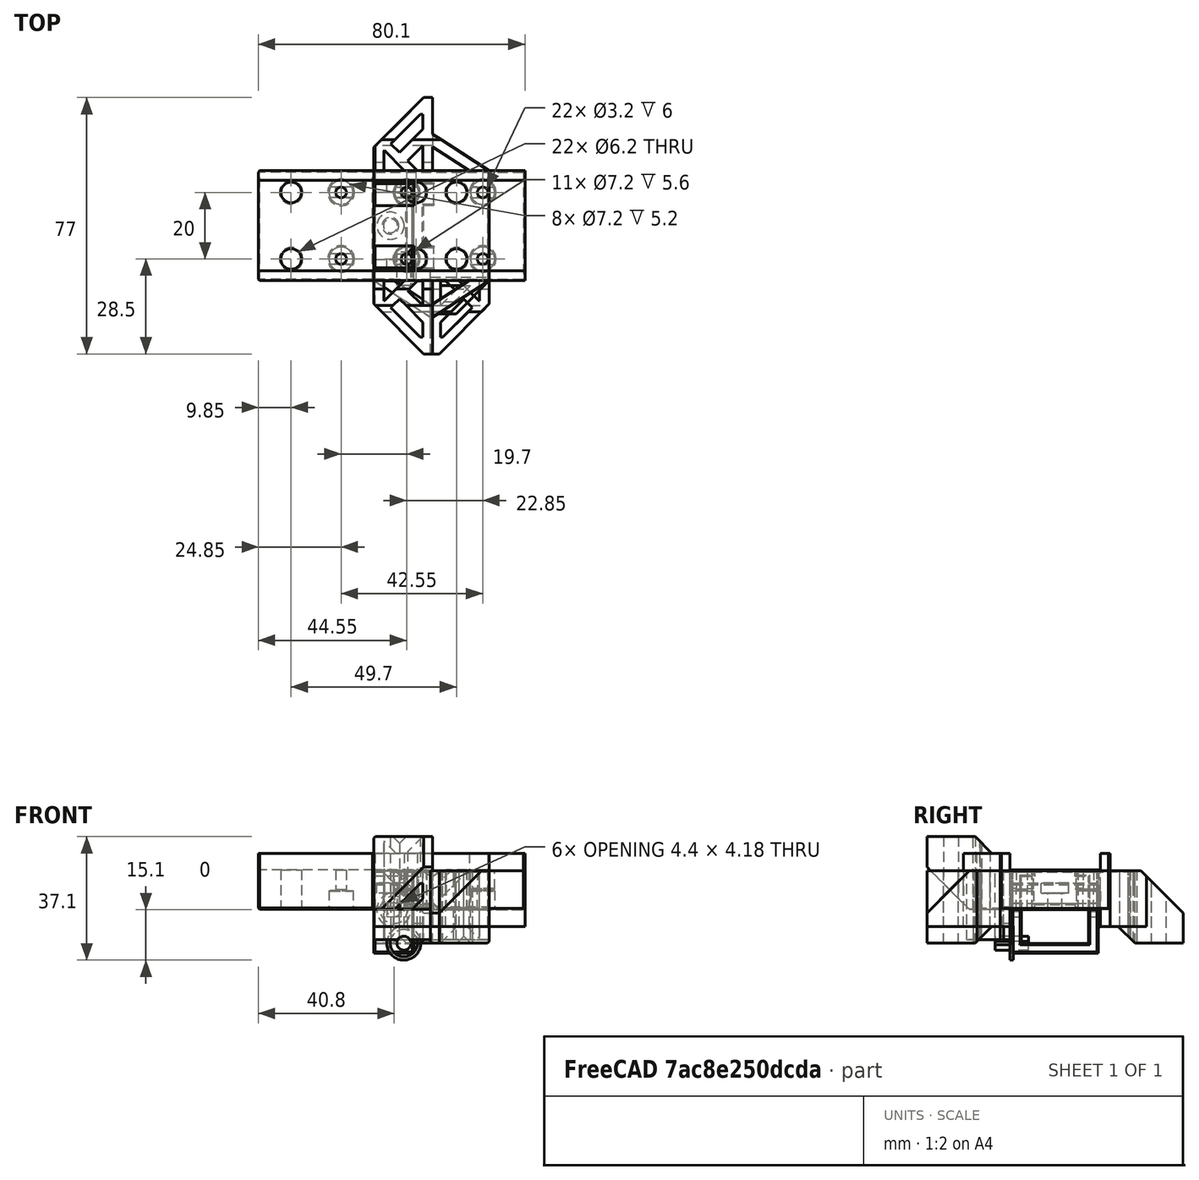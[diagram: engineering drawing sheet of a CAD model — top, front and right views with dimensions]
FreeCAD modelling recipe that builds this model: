
FCSTD DOCUMENT  (FreeCAD 0.18R14555 (Git shallow))
Label: rail-block
License: All rights reserved
LicenseURL: http://en.wikipedia.org/wiki/All_rights_reserved
objects: Part::Box×31, Part::Feature×26, Part::Cut×24, Part::Cylinder×22, Part::MultiFuse×17, Part::Chamfer×15, Part::MultiCommon×1
note: 136 computed .brp shape members not serialized (recipe doc carries the construction recipe); baked Part::Feature solids carry a one-line shape summary decoded from their .brp

FEATURE [Part::Box] Box  label="Cube"
  AttacherType = Attacher::AttachEngine3D
  Height = 2
  Length = 18
  Placement = pos=(0,-13,0) rot=(0,0,1;0rad)
  Width = 26
FEATURE [Part::Box] Box001  label="Cube001"
  AttacherType = Attacher::AttachEngine3D
  Height = 8
  Length = 10
  Placement = pos=(0,-13,0) rot=(0,0,1;0rad)
  Width = 26
FEATURE [Part::Cylinder] Cylinder
  Angle = 360
  AttacherType = Attacher::AttachEngine3D
  Height = 8
  Placement = pos=(5,0,0) rot=(0,0,1;0rad)
  Radius = 2.1
FEATURE [Part::Cylinder] Cylinder001
  Angle = 360
  AttacherType = Attacher::AttachEngine3D
  Height = 3
  Placement = pos=(5,0,5) rot=(0,0,1;0rad)
  Radius = 4.1
FEATURE [Part::Box] Box004  label="Cube004"
  AttacherType = Attacher::AttachEngine3D
  Height = 2
  Length = 3
  Placement = pos=(15,-6.1,0) rot=(0,0,1;0rad)
  Width = 12.2
FEATURE [Part::Box] Box006  label="Cube006"
  AttacherType = Attacher::AttachEngine3D
  Height = 20.2
  Length = 12
  Placement = pos=(0,-10.1,-10.1) rot=(0,0,1;0rad)
  Width = 20.2
FEATURE [Part::Box] Box007  label="Cube007"
  AttacherType = Attacher::AttachEngine3D
  Height = 25
  Length = 12
  Placement = pos=(0,-13,-13) rot=(0,0,1;0rad)
  Width = 26
FEATURE [Part::Cut] Cut002
  Base = -> Box007
  Tool = -> Box006
FEATURE [Part::Box] Box008  label="Cube008"
  AttacherType = Attacher::AttachEngine3D
  Height = 10
  Length = 12
  Placement = pos=(0,-6.05,4) rot=(0,0,1;0rad)
  Width = 12.1
FEATURE [Part::Cut] Cut003
  Base = -> Cut002
  Tool = -> Box008
FEATURE [Part::Cylinder] Cylinder004
  Angle = 360
  AttacherType = Attacher::AttachEngine3D
  Height = 38
  Placement = pos=(6,-18,4e-15) rot=(-1,0,0;1.5708rad)
  Radius = 2.1
FEATURE [Part::Cylinder] Cylinder005
  Angle = 360
  AttacherType = Attacher::AttachEngine3D
  Height = 38
  Placement = pos=(7.8,-18,4e-15) rot=(-1,0,0;1.5708rad)
  Radius = 0.5
FEATURE [Part::MultiFuse] Fusion002
  Shapes = -> [Cylinder004,Cylinder005]
FEATURE [Part::Cut] Cut004  label="node-rev-1-tmp"
  Base = -> Cut003
  Tool = -> Fusion002
FEATURE [Part::Box] Box009  label="Cube009"
  AttacherType = Attacher::AttachEngine3D
  Height = 16.8
  Length = 34.7
  Placement = pos=(0,-16.5,-5) rot=(0,0,1;0rad)
  Width = 33
FEATURE [Part::Box] Box010  label="Cube010"
  AttacherType = Attacher::AttachEngine3D
  Height = 5
  Length = 34.7
  Placement = pos=(0,-13.6,-5) rot=(0,0,1;0rad)
  Width = 27.2
FEATURE [Part::Cylinder] Cylinder006
  Angle = 360
  AttacherType = Attacher::AttachEngine3D
  Height = 12
  Placement = pos=(9.85,10,0) rot=(0,0,1;0rad)
  Radius = 1.6
FEATURE [Part::Cylinder] Cylinder007
  Angle = 360
  AttacherType = Attacher::AttachEngine3D
  Height = 12
  Placement = pos=(9.85,-10,0) rot=(0,0,1;0rad)
  Radius = 1.6
FEATURE [Part::Cylinder] Cylinder008
  Angle = 360
  AttacherType = Attacher::AttachEngine3D
  Height = 12
  Placement = pos=(24.85,10,0) rot=(0,0,1;0rad)
  Radius = 3.1
FEATURE [Part::Cylinder] Cylinder009
  Angle = 360
  AttacherType = Attacher::AttachEngine3D
  Height = 12
  Placement = pos=(24.85,-10,0) rot=(0,0,1;0rad)
  Radius = 3.1
FEATURE [Part::Cylinder] Cylinder010
  Angle = 360
  AttacherType = Attacher::AttachEngine3D
  Height = 6
  Placement = pos=(9.85,-10,6) rot=(0,0,1;0rad)
  Radius = 3.6
FEATURE [Part::Cylinder] Cylinder011
  Angle = 360
  AttacherType = Attacher::AttachEngine3D
  Height = 6
  Placement = pos=(9.85,10,6) rot=(0,0,1;0rad)
  Radius = 3.6
FEATURE [Part::Cylinder] Cylinder012
  Angle = 360
  AttacherType = Attacher::AttachEngine3D
  Height = 10
  Placement = pos=(9,-8,-10) rot=(1,0,0;1.5708rad)
  Radius = 2.1
FEATURE [Part::Cylinder] Cylinder013
  Angle = 360
  AttacherType = Attacher::AttachEngine3D
  Height = 10
  Placement = pos=(10.9,-8,-10) rot=(1,0,0;1.5708rad)
  Radius = 0.5
FEATURE [Part::Cylinder] Cylinder014
  Angle = 360
  AttacherType = Attacher::AttachEngine3D
  Height = 1
  Placement = pos=(9,-12.5,-10) rot=(1,0,0;1.5708rad)
  Radius = 5.1
FEATURE [Part::Cylinder] Cylinder015
  Angle = 360
  AttacherType = Attacher::AttachEngine3D
  Height = 1
  Placement = pos=(9,-12.5,-10) rot=(1,0,0;1.5708rad)
  Radius = 4.1
FEATURE [Part::Cut] Cut
  Base = -> Cylinder014
  Tool = -> Cylinder015
FEATURE [Part::Cylinder] Cylinder016
  Angle = 360
  AttacherType = Attacher::AttachEngine3D
  Height = 1
  Placement = pos=(12.9,-12.5,-10) rot=(1,0,0;1.5708rad)
  Radius = 0.5
FEATURE [Part::Cut] Cut007  label="side-hole-deco"
  Base = -> Cut
  Tool = -> Cylinder016
FEATURE [Part::MultiFuse] Fusion004  label="side-screw-hole"
  Shapes = -> [Cylinder012,Cylinder013]
FEATURE [Part::Cut] Cut007009
  Base = -> Box009
  Tool = -> Box010
FEATURE [Part::Box] Box011  label="Cube011"
  AttacherType = Attacher::AttachEngine3D
  Height = 20.8
  Length = 17.7
  Placement = pos=(17,-26.5,-9) rot=(0,0,1;0rad)
  Width = 11
FEATURE [Part::Box] Box012  label="Cube012"
  AttacherType = Attacher::AttachEngine3D
  Height = 10
  Length = 34.7
  Placement = pos=(0,-16.5,-9) rot=(0,0,1;0rad)
  Width = 2.9
FEATURE [Part::Feature] Body001
  shape: bbox 11 x 9 x 20 mm, 6 faces (baked)
FEATURE [Part::Feature] Body002
  Placement = pos=(0,0,5) rot=(0,0,1;0rad)
  shape: bbox 11 x 9 x 20 mm, 6 faces (baked)
FEATURE [Part::MultiFuse] Fusion004006
  Shapes = -> [Body002,Body001]
FEATURE [Part::Chamfer] Chamfer
  Base = -> Box011
  Edges = 1 edges r=10: [Edge5]
FEATURE [Part::Box] Box013  label="Cube013"
  AttacherType = Attacher::AttachEngine3D
  Height = 31
  Length = 10
  Placement = pos=(15,-33,-18) rot=(0,0,1;0rad)
  Width = 10
FEATURE [Part::Box] Box014  label="Cube014"
  AttacherType = Attacher::AttachEngine3D
  Height = 31
  Length = 10
  Placement = pos=(11,-26,-18) rot=(0,0,1;0rad)
  Width = 10
FEATURE [Part::Cut] Cut007010
  Base = -> Fusion004006
  Tool = -> Box013
FEATURE [Part::Cut] Cut007011
  Base = -> Cut007010
  Placement = pos=(-1,0,0) rot=(0,0,1;0rad)
  Tool = -> Box014
FEATURE [Part::Cut] Cut007012
  Base = -> Chamfer
  Tool = -> Cut007011
FEATURE [Part::MultiFuse] Fusion004007
  Shapes = -> [Cylinder011,Cylinder006,Cylinder007,Cylinder008,Cylinder009,Cylinder010]
FEATURE [Part::Cut] Cut007013  label="block-rev-tmp-1"
  Base = -> Cut007009
  Tool = -> Fusion004007
FEATURE [Part::MultiFuse] Fusion004008
  Shapes = -> [Box,Box001]
FEATURE [Part::Cut] Cut007014
  Base = -> Fusion004008
  Tool = -> Box004
FEATURE [Part::MultiFuse] Fusion
  Shapes = -> [Cylinder,Cylinder001]
FEATURE [Part::Cut] Cut007015  label="head-tail-rev-1"
  Base = -> Cut007014
  Tool = -> Fusion
FEATURE [Part::Box] Box015  label="Cube015"
  AttacherType = Attacher::AttachEngine3D
  Height = 16.8
  Length = 11.7
  Placement = pos=(20,-33.5,-5) rot=(0,0,1;0rad)
  Width = 16.9
FEATURE [Part::Box] Box016  label="Cube016"
  AttacherType = Attacher::AttachEngine3D
  Height = 16.8
  Length = 17.7
  Placement = pos=(17,-38.5,-5) rot=(0,0,1;0rad)
  Width = 24.9
FEATURE [Part::Chamfer] Chamfer001
  Base = -> Box016
  Edges = 1 edges r=15: [Edge5]
FEATURE [Part::Chamfer] Chamfer002
  Base = -> Box015
  Edges = 1 edges r=11: [Edge5]
FEATURE [Part::Cut] Cut007016
  Base = -> Chamfer001
  Tool = -> Chamfer002
FEATURE [Part::Box] Box017  label="Cube017"
  AttacherType = Attacher::AttachEngine3D
  Height = 16.8
  Length = 10
  Placement = pos=(13,-27,-5) rot=(0,0,1;0rad)
  Width = 10
FEATURE [Part::Box] Box018  label="Cube018"
  AttacherType = Attacher::AttachEngine3D
  Height = 16.8
  Length = 15
  Placement = pos=(40,-26,-5) rot=(0,0,1;0rad)
  Width = 18
FEATURE [Part::Box] Box019  label="Cube019"
  AttacherType = Attacher::AttachEngine3D
  Height = 16.8
  Length = 15
  Placement = pos=(40,-26,-5) rot=(0,0,1;0rad)
  Width = 18
FEATURE [Part::Chamfer] Chamfer003
  Base = -> Box018
  Edges = 1 edges r=10: [Edge1]
  Placement = pos=(-20,1,0) rot=(0,0,1;0rad)
FEATURE [Part::Chamfer] Chamfer004
  Base = -> Box019
  Edges = 1 edges r=14: [Edge1]
  Placement = pos=(-20,1,0) rot=(0,0,1;0rad)
FEATURE [Part::Cut] Cut007017
  Base = -> Chamfer003
  Tool = -> Chamfer004
FEATURE [Part::Box] Box020  label="Cube020"
  AttacherType = Attacher::AttachEngine3D
  Height = 16.8
  Length = 10
  Placement = pos=(13,-68,-5) rot=(0,0,1;0rad)
  Width = 12
FEATURE [Part::Chamfer] Chamfer005
  Base = -> Box020
  Edges = 1 edges r=9: [Edge3]
  Placement = pos=(4,38,0) rot=(0,0,1;0rad)
FEATURE [Part::Feature] Chamfer005001  label="Chamfer006"
  Placement = pos=(6,35,0) rot=(0,0,1;0rad)
  shape: bbox 10 x 12 x 16.8 mm, 7 faces (baked)
FEATURE [Part::Cut] Cut007018
  Base = -> Chamfer005
  Tool = -> Chamfer005001
FEATURE [Part::Box] Box021  label="Cube021"
  AttacherType = Attacher::AttachEngine3D
  Height = 16.8
  Length = 10
  Placement = pos=(15,-13.6,-5) rot=(0,0,1;0rad)
  Width = 10
FEATURE [Part::Cut] Cut007019
  Base = -> Cut007017
  Tool = -> Box021
FEATURE [Part::Chamfer] Chamfer005002
  Base = -> Box017
  Edges = 1 edges r=5: [Edge3]
  Placement = pos=(18,-5,0) rot=(0,0,1;0rad)
FEATURE [Part::Cut] Cut007020
  Base = -> Cut007019
  Tool = -> Chamfer005002
FEATURE [Part::MultiFuse] Fusion004009
  Shapes = -> [Cut007020,Cut007016,Cut007018]
FEATURE [Part::Feature] Fusion004009001  label="short-arm"
  shape: bbox 17.7 x 24.9 x 16.8 mm, 20 faces (baked)
FEATURE [Part::Feature] Fusion004009002  label="short-arm001"
  Placement = pos=(0,0,-5) rot=(0,0,1;0rad)
  shape: bbox 17.7 x 24.9 x 16.8 mm, 20 faces (baked)
FEATURE [Part::Box] Box022  label="Cube022"
  AttacherType = Attacher::AttachEngine3D
  Height = 0.2
  Length = 4
  Placement = pos=(1.6,-5,0) rot=(0,0,1;0rad)
  Width = 10
FEATURE [Part::Box] Box023  label="Cube023"
  AttacherType = Attacher::AttachEngine3D
  Height = 0.2
  Length = 4
  Placement = pos=(-5.6,-5,0) rot=(0,0,1;0rad)
  Width = 10
FEATURE [Part::Box] Box024  label="Cube024"
  AttacherType = Attacher::AttachEngine3D
  Height = 0.4
  Length = 8
  Placement = pos=(-4,-6.6,0) rot=(0,0,1;0rad)
  Width = 5
FEATURE [Part::Box] Box025  label="Cube025"
  AttacherType = Attacher::AttachEngine3D
  Height = 0.4
  Length = 8
  Placement = pos=(-4,1.6,0) rot=(0,0,1;0rad)
  Width = 5
FEATURE [Part::Cylinder] Cylinder017
  Angle = 360
  AttacherType = Attacher::AttachEngine3D
  Height = 10
  Radius = 3.7
FEATURE [Part::MultiFuse] Fusion004009004
  Shapes = -> [Box025,Box023,Box024,Box022]
FEATURE [Part::MultiCommon] Common  label="screw-hole-support"
  Placement = pos=(9.85,10,6) rot=(0,0,1;0rad)
  Shapes = -> [Cylinder017,Fusion004009004]
FEATURE [Part::Feature] Common001  label="screw-hole-support001"
  shape: bbox 7.4 x 7.4 x 0.4 mm, 10 faces (baked)
FEATURE [Part::Feature] Common002  label="screw-hole-support002"
  Placement = pos=(0,-20,0) rot=(0,0,1;0rad)
  shape: bbox 7.4 x 7.4 x 0.4 mm, 10 faces (baked)
FEATURE [Part::MultiFuse] Fusion004009005  label="block-rev-1"
  Shapes = -> [Common001,Common002,Cut007013]
FEATURE [Part::Box] Box026  label="Cube026"
  AttacherType = Attacher::AttachEngine3D
  Height = 6
  Length = 6
  Placement = pos=(12,-16.5,-10) rot=(0,0,1;0rad)
  Width = 2.9
FEATURE [Part::Box] Box027  label="Cube027"
  AttacherType = Attacher::AttachEngine3D
  Height = 16.8
  Length = 17
  Placement = pos=(0,-28,-5) rot=(0,0,1;0rad)
  Width = 12
FEATURE [Part::Box] Box028  label="Cube028"
  AttacherType = Attacher::AttachEngine3D
  Height = 16.8
  Length = 34
  Placement = pos=(-10.4225,-24.0104,-5) rot=(0,0,-1;0.575959rad)
  Width = 12
FEATURE [Part::Cut] Cut007021
  Base = -> Box027
  Tool = -> Box028
FEATURE [Part::Feature] Cut007021001  label="Cut007022"
  Placement = pos=(6,0,0) rot=(0,0,1;0rad)
  shape: bbox 17 x 11.51 x 16.8 mm, 6 faces (baked)
FEATURE [Part::Cut] Cut007021002
  Base = -> Cut007021
  Tool = -> Cut007021001
FEATURE [Part::Box] Box029  label="Cube029"
  AttacherType = Attacher::AttachEngine3D
  Height = 16
  Length = 36
  Placement = pos=(0,-20,-9) rot=(0,0,1;0rad)
  Width = 15
FEATURE [Part::Chamfer] Chamfer005004  label="cut"
  Base = -> Box029
  Edges = 1 edges r=9: [Edge10]
  Placement = pos=(0,-8,-12) rot=(0,0,1;0rad)
FEATURE [Part::Box] Box030  label="Cube030"
  AttacherType = Attacher::AttachEngine3D
  Height = 29
  Length = 39
  Placement = pos=(0,-41,27) rot=(0,0,1;0rad)
  Width = 38
FEATURE [Part::Chamfer] Chamfer005006
  Base = -> Box026
  Edges = 1 edges r=5: [Edge4]
FEATURE [Part::MultiFuse] Fusion004009006
  Shapes = -> [Chamfer005006,Fusion004009002,Cut007021002,Fusion004009001]
FEATURE [Part::Cut] Cut007021003
  Base = -> Fusion004009006
  Tool = -> Chamfer005004
FEATURE [Part::Chamfer] Chamfer005007
  Base = -> Box030
  Edges = 1 edges r=20: [Edge11]
  Placement = pos=(0,-15.6,-28) rot=(0,0,1;0rad)
FEATURE [Part::Cut] Cut007021004  label="arm-rev-1"
  Base = -> Cut007021003
  Tool = -> Chamfer005007
FEATURE [Part::Feature] Cut007021004001  label="arm-rev-002"
  shape: bbox 34.7 x 24.9 x 21.8 mm, 33 faces (baked)
FEATURE [Part::Feature] Fusion004009005001  label="block-rev-002"
  shape: bbox 34.7 x 33 x 16.8 mm, 40 faces (baked)
FEATURE [Part::MultiFuse] Fusion004009005002
  Shapes = -> [Cut007021004001,Fusion004009005001]
FEATURE [Part::Feature] Fusion004009005002002  label="block-rev-1-tmp"
  shape: bbox 34.7 x 33 x 16.8 mm, 40 faces (baked)
FEATURE [Part::Feature] Cut007015001  label="head-tail-rev-1-tmp"
  shape: bbox 18 x 26 x 8 mm, 15 faces (baked)
FEATURE [Part::Chamfer] Chamfer005010  label="head-tail-rev-1-exp"
  Base = -> Cut007015001
  Edges = 20 edges r=0.4: [Edge1,Edge2,Edge3,Edge4,Edge6,Edge7,Edge13,Edge15,Edge16,Edge17,Edge18,Edge24,Edge27,Edge28,Edge31,Edge32,Edge33,Edge34,Edge35,Edge36]
FEATURE [Part::Chamfer] Chamfer005012  label="block-12C-rev-1-exp"
  Base = -> Fusion004009005002002
  Edges = 12 edges r=0.4: [Edge23,Edge35,Edge36,Edge37,Edge38,Edge39,Edge40,Edge41,Edge45,Edge51,Edge53,Edge55]
FEATURE [Part::Feature] Chamfer005010_solid  label="head-tail-rev-1-exp (Solid)"
  shape: bbox 18 x 26 x 8 mm, 41 faces (baked)
FEATURE [Part::Feature] Chamfer005012_solid  label="block-rev-1-exp (Solid)"
  Placement = pos=(-1e-15,0,12) rot=(0,1,0;3.14159rad)
  shape: bbox 34.7 x 33 x 16.8 mm, 56 faces (baked)
FEATURE [Part::Feature] Fusion004009005002003  label="block-rev-003"
  shape: bbox 34.7 x 33 x 16.8 mm, 40 faces (baked)
FEATURE [Part::Feature] Cut007021004002  label="arm-rev-003"
  Placement = pos=(34.7,-5e-15,0) rot=(0,0,1;3.14159rad)
  shape: bbox 34.7 x 24.9 x 21.8 mm, 70 faces (baked)
FEATURE [Part::MultiFuse] Fusion004009005002004
  Shapes = -> [Fusion004009005002003,Cut007021004002]
FEATURE [Part::Feature] Fusion004009005002004001  label="Fusion004009005002005"
  shape: bbox 34.7 x 55 x 21.8 mm, 63 faces (baked)
FEATURE [Part::Chamfer] Chamfer005013
  Base = -> Fusion004009005002004001
  Edges = 9 edges r=0.4: [Edge11,Edge75,Edge77,Edge85,Edge86,Edge87,Edge93,Edge102,Edge106]
FEATURE [Part::Feature] Chamfer005013001  label="block-w-arm-rev-exp"
  Placement = pos=(0,1e-15,12) rot=(1,0,0;3.14159rad)
  shape: bbox 34.7 x 55 x 21.8 mm, 75 faces (baked)
FEATURE [Part::Box] Box031  label="Cube031"
  AttacherType = Attacher::AttachEngine3D
  Height = 11.8
  Length = 45.4
  Placement = pos=(0,-16.5,0) rot=(0,0,1;0rad)
  Width = 33
FEATURE [Part::Box] Box032  label="Cube032"
  AttacherType = Attacher::AttachEngine3D
  Height = 5
  Length = 45.4
  Placement = pos=(0,-16.5,-5) rot=(0,0,1;0rad)
  Width = 2.9
FEATURE [Part::Box] Box033  label="Cube033"
  AttacherType = Attacher::AttachEngine3D
  Height = 5
  Length = 45.4
  Placement = pos=(0,13.6,-5) rot=(0,0,1;0rad)
  Width = 2.9
FEATURE [Part::Cylinder] Cylinder018
  Angle = 360
  AttacherType = Attacher::AttachEngine3D
  Height = 15
  Placement = pos=(12.7,-10,0) rot=(0,0,1;0rad)
  Radius = 3.1
FEATURE [Part::Cylinder] Cylinder019
  Angle = 360
  AttacherType = Attacher::AttachEngine3D
  Height = 6
  Placement = pos=(32.7,-10,0) rot=(0,0,1;0rad)
  Radius = 3.6
FEATURE [Part::Cylinder] Cylinder020
  Angle = 360
  AttacherType = Attacher::AttachEngine3D
  Height = 6
  Placement = pos=(32.7,10,0) rot=(0,0,1;0rad)
  Radius = 3.6
FEATURE [Part::Cylinder] Cylinder021
  Angle = 360
  AttacherType = Attacher::AttachEngine3D
  Height = 15
  Placement = pos=(12.7,10,0) rot=(0,0,1;0rad)
  Radius = 3.1
FEATURE [Part::MultiFuse] Fusion004009005002004002
  Shapes = -> [Cylinder021,Cylinder018]
FEATURE [Part::Cylinder] Cylinder022
  Angle = 360
  AttacherType = Attacher::AttachEngine3D
  Height = 15
  Placement = pos=(32.7,-10,0) rot=(0,0,1;0rad)
  Radius = 1.6
FEATURE [Part::Cylinder] Cylinder023
  Angle = 360
  AttacherType = Attacher::AttachEngine3D
  Height = 15
  Placement = pos=(32.7,10,0) rot=(0,0,1;0rad)
  Radius = 1.6
FEATURE [Part::MultiFuse] Fusion004009005002004003
  Shapes = -> [Cylinder022,Cylinder023]
FEATURE [Part::MultiFuse] Fusion004009005002004004
  Placement = pos=(0,0,6) rot=(0,0,1;0rad)
  Shapes = -> [Cylinder019,Cylinder020]
FEATURE [Part::Feature] Common003  label="screw-hole-support003"
  Placement = pos=(22.85,0,0) rot=(0,0,1;0rad)
  shape: bbox 7.4 x 7.4 x 0.4 mm, 10 faces (baked)
FEATURE [Part::Feature] Common004  label="screw-hole-support004"
  Placement = pos=(22.85,-20,0) rot=(0,0,1;0rad)
  shape: bbox 7.4 x 7.4 x 0.4 mm, 10 faces (baked)
FEATURE [Part::Feature] Fusion004009005002004005001  label="block-12h-rev-002"
  shape: bbox 45.4 x 33 x 16.9 mm, 40 faces (baked)
FEATURE [Part::Chamfer] Chamfer005013002
  Base = -> Fusion004009005002004005001
  Edges = 12 edges r=0.4: [Edge1,Edge2,Edge3,Edge4,Edge5,Edge6,Edge7,Edge8,Edge101,Edge102,Edge103,Edge104]
  Placement = pos=(0,1e-15,12) rot=(1,0,0;3.14159rad)
FEATURE [Part::Feature] Chamfer005013002_solid  label="block-12h-rev-1-exp"
  shape: bbox 45.4 x 33 x 16.9 mm, 56 faces (baked)
FEATURE [Part::Feature] Fusion004005001  label="node-rev-1-w-aliner"
  shape: bbox 12 x 27 x 25 mm, 28 faces (baked)
FEATURE [Part::Chamfer] Chamfer005013003  label="node-rev-1"
  Base = -> Cut004
  Edges = 25 edges r=0.4: [Edge1,Edge3,Edge4,Edge5,Edge6,Edge7,Edge9,Edge10,Edge11,Edge12,Edge14,Edge15,Edge16,Edge18,Edge21,Edge26,Edge27,Edge32,Edge34,Edge36,Edge38,Edge39,Edge43,Edge44,Edge45]
FEATURE [Part::Feature] Chamfer005013003001  label="node-rev-1-exp"
  shape: bbox 12 x 26 x 25 mm, 50 faces (baked)
FEATURE [Part::Feature] Fusion004009005002004005002  label="Fusion004009005002004005"
  shape: bbox 34.7 x 55 x 21.8 mm, 63 faces (baked)
FEATURE [Part::MultiFuse] Fusion004009005002004005003
  Shapes = -> [Box031,Box033,Box032]
FEATURE [Part::Cut] Cut007021004003
  Base = -> Fusion004009005002004005003
  Tool = -> Fusion004009005002004002
FEATURE [Part::Cut] Cut007021004004
  Base = -> Cut007021004003
  Tool = -> Fusion004009005002004003
FEATURE [Part::Cut] Cut007021004005
  Base = -> Cut007021004004
  Tool = -> Fusion004009005002004004
FEATURE [Part::MultiFuse] Fusion004009005002004005004
  Shapes = -> [Common003,Common004,Cut007021004005]
FEATURE [Part::Feature] Fusion004009005002004005004001  label="Fusion004009005002004005005"
  shape: bbox 45.4 x 33 x 16.8 mm, 40 faces (baked)
